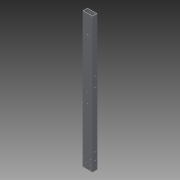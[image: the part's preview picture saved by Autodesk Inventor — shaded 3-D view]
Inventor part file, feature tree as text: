
AUTODESK INVENTOR PART (.ipt)
format: ipt  version: 2013 (Build 170138000, 138)  size: 195,072 bytes
history: native  units: in
note: dims shown in document units (in); Inventor stores cm internally (conversion verified against a paired STEP export)
features: sketch x9, extrude x8, hole x1
ambient origin geometry x8: Origin, YZ Plane, XZ Plane, XY Plane, X Axis, Y Axis, Z Axis, Center Point
bodies: Solid1 (feature_tree)
feature tree (18):
  extrude  "Extrusion1"  Depth=1.0in
  extrude  "Extrusion2"  Depth=0.75in
  extrude  "Extrusion3"  Depth=1.0in
  extrude  "Extrusion4"  Depth=0.5in
  extrude  "Extrusion5"  Depth=2.0in
  extrude  "Extrusion6"  Depth=2.0in
  extrude  "Extrusion8"  Depth=0.5in
  extrude  "Extrusion9"  Depth=1.0in
  hole  "Hole1"  [1 undecoded]
  sketch  "Sketch1"  dims[d0=2.0in d1=1.0in]
  sketch  "Sketch2"  dims[d2=1.75in d3=0.75in]
  sketch  "Sketch3"  dims[d4=24.0in d5=0.0in d6=1.0in]
  sketch  "Sketch4"  dims[d7=1.0in d8=0.5in]
  sketch  "Sketch5"  dims[d9=24.0in d10=0.0in d11=2.0in]
  sketch  "Sketch6"  dims[d12=2.0in d13=2.0in]
  sketch  "Sketch7"  dims[d14=1.0in d15=0.5in]
  sketch  "Sketch8"  dims[d16=0.5in d17=1.0in]
  sketch  "Sketch9"  dims[d18=1.0in d19=0.25in d20=0.25in d21=0.25in d22=0.25in d23=24.0in d24=0.0in d25=0.5in d26=0.0in d27=0.75in d28=90.0deg d29=1.0in d30=90.0deg d31=0.2in d32=0.2in d33=1.0in d34=0.0in d35=2.5in d36=0.0in d37=10.5in d38=90.0deg d39=0.25in d40=2.0in d41=2.0in d42=90.0deg d43=0.25in d44=0.25in d47=2.0in d48=0.0in d49=13.543in d50=90.0deg d51=2.0in d52=180.0deg d53=0.25in d54=0.25in d55=2.0in d56=0.0in d57=3.313in d58=1.5in d59=90.0deg d60=0.25in d61=0.75in d62=0.375in d63=0.25in d64=0.5635in d65=1.0in d66=0.8108in]
note: 1 required parameter value undecoded (feature->parameter linkage not recoverable at this tier; creation-order binding heuristic only, values carry confidence <= 0.55)
